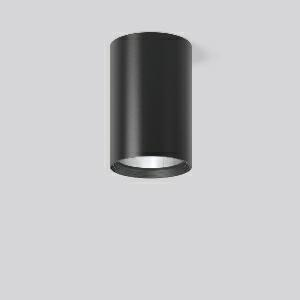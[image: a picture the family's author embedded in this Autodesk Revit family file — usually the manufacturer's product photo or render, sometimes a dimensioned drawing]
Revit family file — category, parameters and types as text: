
# Revit family: heledon_maxi_a_931230_003_76_0dff
name_source: partatom
category: Lighting Fixtures
units: mm (PartAtom-declared; Revit-internal decimal feet)

## family parameters
Cut with Voids When Loaded = No
Host = Face
Light Source = No
Part Type = Normal
Room Calculation Point = No
Round Connector Dimension = Use Diameter
Shared = No

## types (1)
- HELEDON maxi A (1 x LED Modul 932 fresh meat, 2100 lm, 3200)
    Apparent Load = 33 VA
    Approval mark = CE
    CIE Flux Codes = 100 100 100 100 100
    Color Rendering = 90
    Color Temperature = 3200
    Default Elevation = 1800 mm
    Description = Series: HELEDON maxi
Cylindrical surface-mounted downlight. Housing: die-cast aluminium, powder-coated. Internal ceiling frame polycarbonate with bayonet mounting. Black plastic ring and recessed LED to prevent glare from the side. Optical assembly with reflector made of MIRO-Silver with 98% total light reflection for outstanding efficiency - can be changed without tools. Special LED for illumination of meat included. Suitable for Ceiling mounting. Easy installation with a separate ceiling frame with bayonet mounting and plug connection. Driver integrated. Connected via plug-in connector. High quality converter without flickering and stroboscopic effect. The following accessories can be mounted without use of tools: interchangeable lenses, decorative glasses, honeycomb louvre, clear and frosted diffusers, white interchangeable plastic ring. 
Colour: deep black, matt (RAL 9005)
Diameter: 123 mm
Height: 183 mm
Lamp: LED
Socket: without socket
Colour temperature: fresh meat
System power: 33 W
Rated luminous flux: 2100 lm
Luminous efficiency: 64 lm/W
Control gear: Converter, dimmable, DALI
Protection class: I
Type of protection: IP 20
    Height = 183 mm
    Lamp = 1 x LED Modul 932 fresh meat
    Lamp Light Flux = 2100 lm
    Lamp count = 1
    Length = 123 mm
    Lifetime = 50000 h
    Luminous efficacy = 64 lm/W
    Manufacturer = RZB
    ModVariant = No
    Model = 931230.003.76
    Mounting Place = Ceiling
    Mounting Type = Surface mounted
    Number of Poles = 1
    OnlyDefault = Yes
    Power Factor = 1
    Product Name = HELEDON maxi A
    Product group = Surface mounted downlights
    ProductGroupID = 302
    Protection Class = Protection class I
    Protection Degree = IP 20
    RLX_Detail_Level = 1
    RLX_Emergency_Light_Flux = 0 lm
    RLX_Emergency_Type = 0
    RLX_Emergency_Type_DB = No
    RlxData = <blob elided: 97673 chars, md5=c16b1db5>
    Socket = socket
    Standby Power = 0 W
    System Light Flux = 2100 lm
    System Power = 33 W
    Type Comments = Product without accessories
    Type Image = 931192.003.jpg
    URL = http://relux.com
    VarID = ---
    Voltage = 230 V
    Voltage Range = 220-240 V
    Weight = 0.00 kg
    Width = 0 mm  [stored 0 ft]

note: [stored X ft] marks values corroborated as IEEE doubles in the binary element streams (Revit-internal decimal feet)

## geometry (parser evidence)
native form markers: Blend x4, Sweep x11
no freeform markers — native parametric forms only
